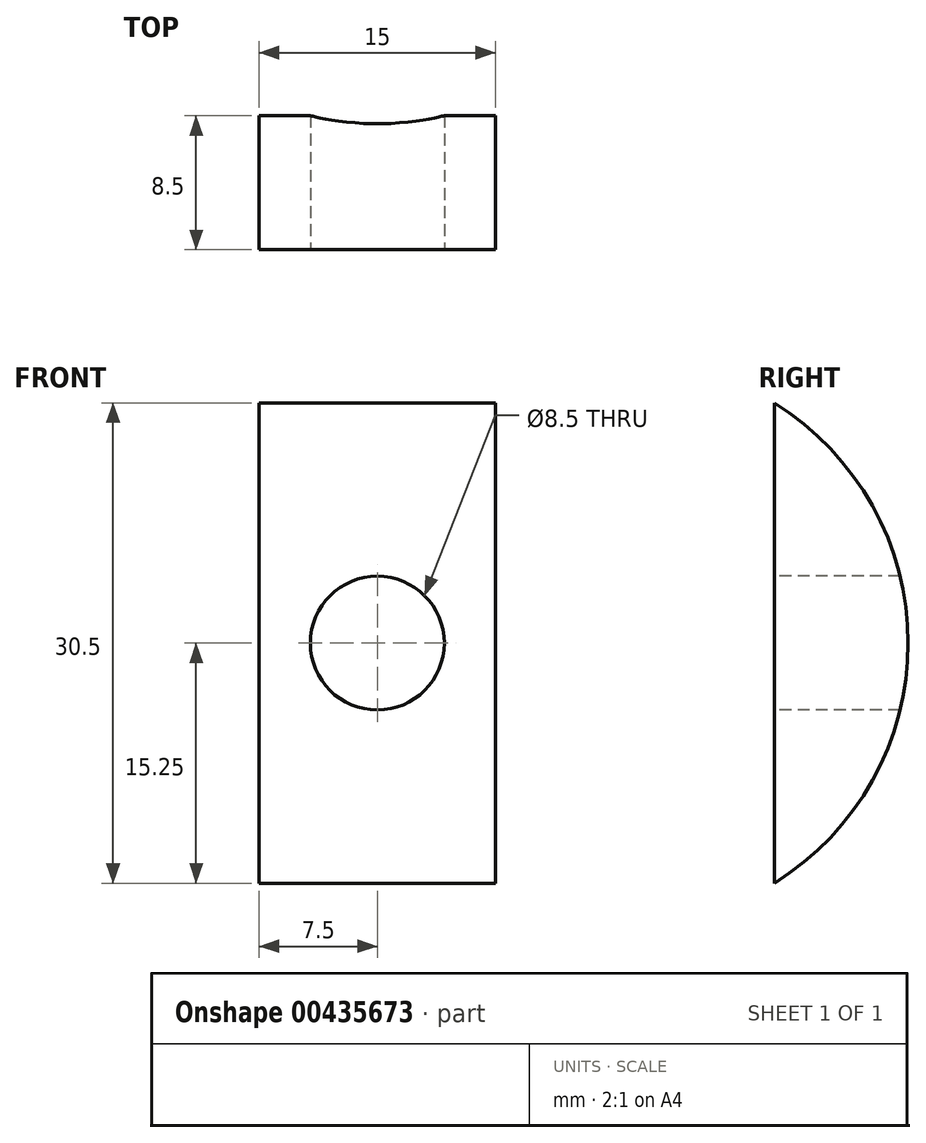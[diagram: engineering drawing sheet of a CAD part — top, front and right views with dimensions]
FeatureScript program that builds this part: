
annotation { "Feature Type Name" : "Feature", "Feature Type Description" : "" }
export const myFeature = defineFeature(function(context is Context, id is Id, definition is map)
    precondition{}
    {
        {
            var Q0;
            Q0=qCreatedBy(makeId("Right.planeOp"),FACE);
            var sketch = newSketch(context, id + "F0", { "sketchPlane" : qUnion([Q0])});
            skLineSegment(sketch, "E0", {"start": v(0, 15.25) * mm, "end": v(0, -15.25) * mm});
            skArc(sketch, "E1", {"start": v(0, -15.25) * mm, "mid": v(8.5, 0) * mm, "end": v(0, 15.25) * mm});
            skSolve(sketch);
        }
        {
            var Q0;
            Q0 = qSketchRegion(id + "F0", true);
            extrude(context, id + "F1", {"entities" : qUnion([Q0]), "depth" : 15 * mm});
        }
        {
            var Q0;
            Q0=makeQuery(id+"F1.opExtrude","SWEPT_FACE",FACE,{"disambiguationData":[OSD([sQuery(id+"F0.wireOp",EDGE,"E0")])]});
            var sketch = newSketch(context, id + "F2", { "sketchPlane" : qUnion([Q0])});
            skCircle(sketch, "E2", {"center": v(7.5, 0) * mm, "radius": 4.25 * mm});
            skPoint(sketch, "E2.centerSnap0", {"position": v(15, 0) * mm});
            skPoint(sketch, "E2.centerSnap1", {"position": v(7.5, 15.25) * mm});
            skSolve(sketch);
        }
        {
            var Q0;
            Q0 = qSketchRegion(id + "F2", true);
            extrude(context, id + "F3", {"entities" : qUnion([Q0]), "operationType" : NewBodyOperationType.REMOVE, "oppositeDirection" : true, "depth" : 25 * mm});
        }
    });
